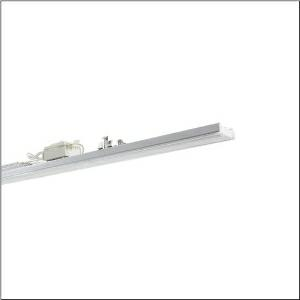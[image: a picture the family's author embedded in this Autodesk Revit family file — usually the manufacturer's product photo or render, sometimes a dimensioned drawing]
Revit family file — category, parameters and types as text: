
# Revit family: licross_21_recessed_mo_52tl12dv4fxg3c
name_source: partatom
category: Lighting Fixtures
units: mm (PartAtom-declared; Revit-internal decimal feet)

## family parameters
Cut with Voids When Loaded = No
Host = Face
Light Source = No
Part Type = Normal
Room Calculation Point = No
Round Connector Dimension = Use Diameter
Shared = No

## types (1)
- --- (1 x LED, 950 lm, 5.5 W, 4000K)
    Apparent Load = 6 VA
    CIE Flux Codes = 72 92 99 100 100
    Color Rendering = 80
    Color Temperature = 4000K
    Default Elevation = 1800 mm
    Description = Licross 21 Recessed MO, luminaire insert, of sheet steel, galvanised, coil coated, white, length: 2.250mm, width: 66mm, height: 67mm, LED rated luminous flux: 15.420lm, light colour: 840, SDCM (Standard Deviation of Colour Matching)MacAdam ≤ 3 SDCM (initial), control gear: DALI 2 (for two DALI lines), with plug, 6-pole, with phase selection, for trunking rail, 14-core, mains connection: 220..240V, AC, 50/60Hz, rated input power: 89W, for trunking rail, 14-core, internal wiring halogen-free, for emergency light function, converter,control gear: single battery element, battery: LiFePO4, 9Ah, primary optical cover: cover, of PMMA, light emission: direct distribution, primary light characteristic: symmetric, protection rating (complete): IP40, insulation class (complete): insulation class I (protective earthing), certification: CE, UKCA, protection symbol: D if used in an environment without relevant dust loads with corresponding accessories, impact resistance: IK06, permissible ambient temperature for indoor applications: +5..+35°C, standard: EN 60598-2-22, LABS conformity tested according to VDMA 24364:2018-05, reducing of maximum allowable ambient temperature of 5°C with ceiling mounting, corresponds to IFS (International Featured Standards) requirements for safety and quality in the food industry, The light source and the operating device comply with the requirements of the Ecodesign Regulation (EU) 2019/2020 and are replaceable in accordance with this regulation, packaging unit: 1 piece
    Height = 58 mm
    Lamp = 1 x LED
    Lamp Light Flux = 950 lm
    Lamp Power = 5.5 W
    Lamp count = 1
    Length = 2250 mm
    Luminous efficacy = 173 lm/W
    Manufacturer = Siteco
    ModVariant = No
    Model = 52TL12DV4FXG3C
    Mounting Place = Ceiling
    Mounting Type = Pendant
    Number of Poles = 1
    OnlyDefault = Yes
    Power Factor = 1
    Product Name = Licross 21 Recessed MO
    Product group = luminaire insert | ceiling pendant
    ProductGroupID = 901
    Protection Class = Protection class I
    Protection Degree = IP 40
    RLX_Detail_Level = 1
    RLX_Emergency_Light_Flux = 0 lm
    RLX_Emergency_Type = 0
    RLX_Emergency_Type_DB = No
    RlxData = <blob elided: 30337 chars, md5=d1f733d1>
    Socket = socket
    Standby Power = 0 W
    System Light Flux = 950 lm
    System Power = 6 W
    Type Comments = : emergency light operation: 3 h
    Type Image = l_1296930.jpg
    URL = http://relux.com
    VarID = @adj_110015
    Voltage = 0 V
    Weight = 0.00 kg
    Width = 66 mm

## geometry (parser evidence)
native form markers: Blend x4, Sweep x10
no freeform markers — native parametric forms only
